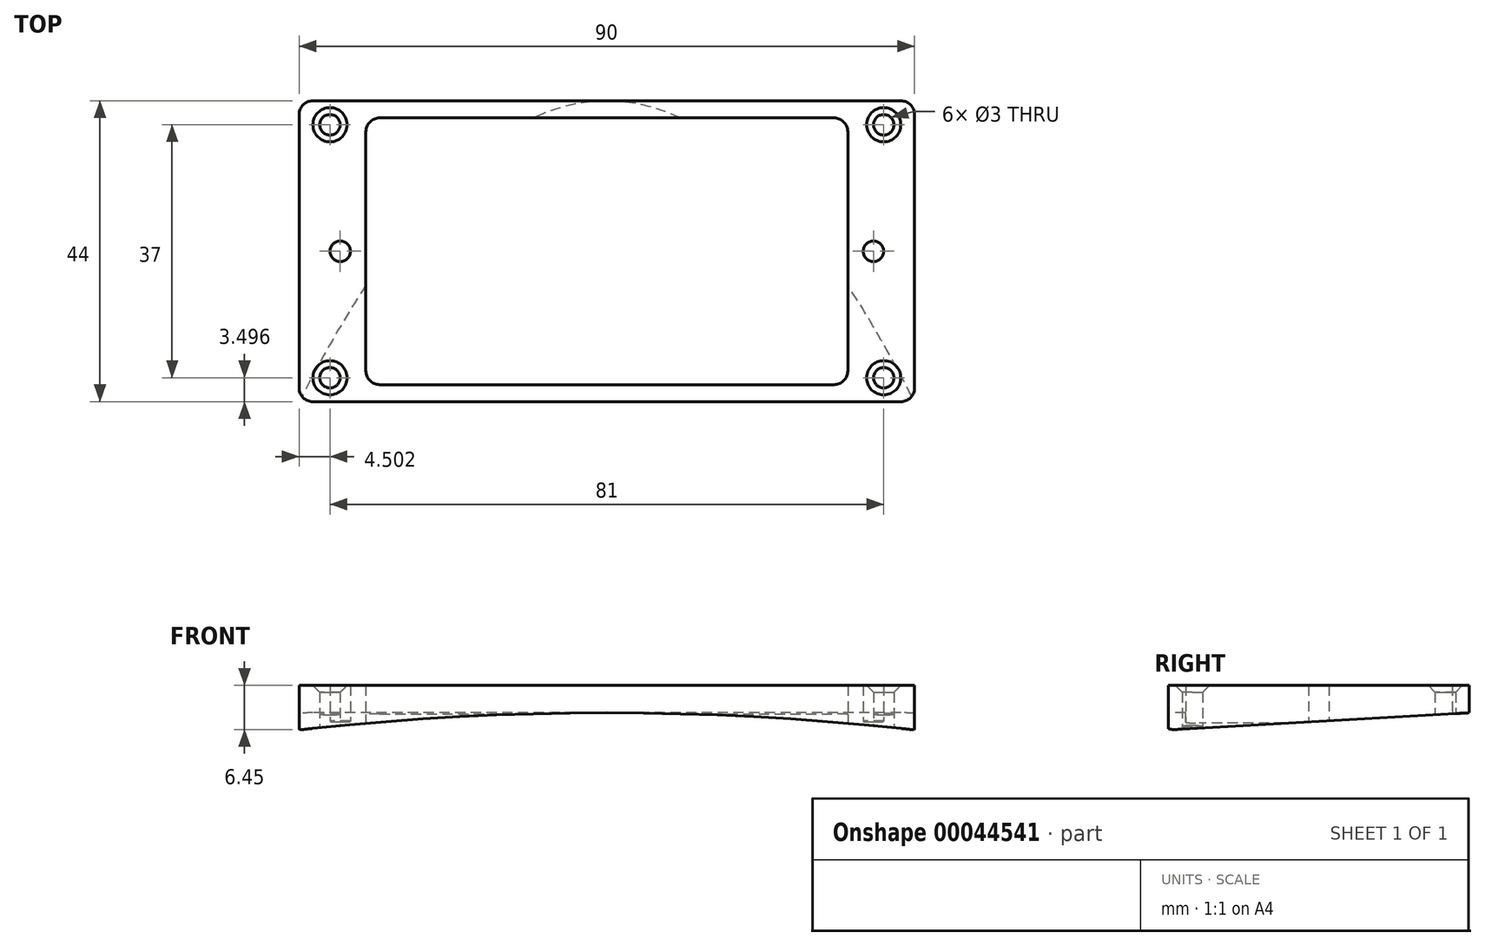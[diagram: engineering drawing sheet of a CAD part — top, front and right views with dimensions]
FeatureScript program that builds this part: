
annotation { "Feature Type Name" : "Feature", "Feature Type Description" : "" }
export const myFeature = defineFeature(function(context is Context, id is Id, definition is map)
    precondition{}
    {
        {
            var Q0;
            Q0=qCreatedBy(makeId("Top.planeOp"),FACE);
            var sketch = newSketch(context, id + "F0", { "sketchPlane" : qUnion([Q0])});
            skLineSegment(sketch, "E0.bottom", {"start": v(-26.2, 30.05) * mm, "end": v(63.8, 30.05) * mm});
            skLineSegment(sketch, "E0.top", {"start": v(-26.2, -13.95) * mm, "end": v(63.8, -13.95) * mm});
            skLineSegment(sketch, "E0.left", {"start": v(-26.2, 30.05) * mm, "end": v(-26.2, -13.95) * mm});
            skLineSegment(sketch, "E0.right", {"start": v(63.8, 30.05) * mm, "end": v(63.8, -13.95) * mm});
            skLineSegment(sketch, "E1.bottom", {"start": v(-16.45, 27.55) * mm, "end": v(54.05, 27.55) * mm});
            skLineSegment(sketch, "E1.top", {"start": v(-16.45, -11.45) * mm, "end": v(54.05, -11.45) * mm});
            skLineSegment(sketch, "E1.left", {"start": v(-16.45, 27.55) * mm, "end": v(-16.45, -11.45) * mm});
            skLineSegment(sketch, "E1.right", {"start": v(54.05, 27.55) * mm, "end": v(54.05, -11.45) * mm});
            skCircle(sketch, "E2", {"center": v(-21.7, 26.55) * mm, "radius": 1.5 * mm});
            skCircle(sketch, "E3", {"center": v(-21.7, -10.45) * mm, "radius": 1.5 * mm});
            skCircle(sketch, "E4", {"center": v(59.3, -10.45) * mm, "radius": 1.5 * mm});
            skCircle(sketch, "E5", {"center": v(59.3, 26.55) * mm, "radius": 1.5 * mm});
            skPoint(sketch, "E6", {"position": v(18.8, 30.05) * mm});
            skLineSegment(sketch, "E7", {"start": v(18.8, 30.05) * mm, "end": v(18.8, -22.23) * mm, "construction": true});
            skPoint(sketch, "E8", {"position": v(18.8, 27.55) * mm});
            skPoint(sketch, "E9", {"position": v(-26.2, 8.05) * mm});
            skLineSegment(sketch, "E10", {"start": v(-26.2, 8.05) * mm, "end": v(76.5, 8.05) * mm, "construction": true});
            skCircle(sketch, "E11", {"center": v(-20.2, 8.05) * mm, "radius": 1.5 * mm});
            skCircle(sketch, "E12", {"center": v(57.8, 8.05) * mm, "radius": 1.5 * mm});
            skPoint(sketch, "E13", {"position": v(-16.45, 8.05) * mm});
            skSolve(sketch);
        }
        {
            var Q0;
            Q0=makeQuery(id+"F0.imprint","IMPRINT",FACE,{"disambiguationData":[TD([[makeQuery(id+"F0.imprint","IMPRINT",EDGE,{"derivedFrom":sQuery(id+"F0.wireOp",EDGE,"E0.bottom")}),-1.0]])]});
            extrude(context, id + "F1", {"entities" : qUnion([Q0]), "depth" : 6.5 * mm});
        }
        {
            var Q0;
            Q0=makeQuery(id+"F1.opExtrude","SWEPT_FACE",FACE,{"disambiguationData":[OSD([sQuery(id+"F0.wireOp",EDGE,"E0.top")])]});
            var sketch = newSketch(context, id + "F2", { "sketchPlane" : qUnion([Q0])});
            skLineSegment(sketch, "E14", {"start": v(-26.2, 0) * mm, "end": v(63.8, 0) * mm});
            skLineSegment(sketch, "E15", {"start": v(-26.2, 2.5) * mm, "end": v(63.8, 2.5) * mm, "construction": true});
            skPoint(sketch, "E16", {"position": v(18.8, 2.5) * mm});
            skArc(sketch, "E17", {"start": v(63.8, 0) * mm, "mid": v(18.8, 2.5) * mm, "end": v(-26.2, 0) * mm});
            skSolve(sketch);
        }
        {
            var Q0;
            Q0=makeQuery(id+"F2.imprint","IMPRINT",FACE,{"disambiguationData":[TD([[makeQuery(id+"F2.imprint","IMPRINT",EDGE,{"derivedFrom":sQuery(id+"F2.wireOp",EDGE,"E14")}),1.0]])]});
            extrude(context, id + "F3", {"entities" : qUnion([Q0]), "operationType" : NewBodyOperationType.REMOVE, "endBound" : BoundingType.THROUGH_ALL, "oppositeDirection" : true, "depth" : 25 * mm});
        }
        {
            var Q0;
            Q0=makeQuery(id+"F1.opExtrude","CAP_EDGE",EDGE,{"disambiguationData":[OSD([sQuery(id+"F0.wireOp",EDGE,"E5")])],"isStart":false});
            var Q1;
            Q1=makeQuery(id+"F1.opExtrude","CAP_EDGE",EDGE,{"disambiguationData":[OSD([sQuery(id+"F0.wireOp",EDGE,"E2")])],"isStart":false});
            var Q2;
            Q2=makeQuery(id+"F1.opExtrude","CAP_EDGE",EDGE,{"disambiguationData":[OSD([sQuery(id+"F0.wireOp",EDGE,"E3")])],"isStart":false});
            var Q3;
            Q3=makeQuery(id+"F1.opExtrude","CAP_EDGE",EDGE,{"disambiguationData":[OSD([sQuery(id+"F0.wireOp",EDGE,"E4")])],"isStart":false});
            chamfer(context, id + "F4", {"entities" : qUnion([Q0, Q1, Q2, Q3]), "width" : 1 * mm, "tangentPropagation" : true});
        }
        {
            var Q0;
            Q0=makeQuery(id+"F1.opExtrude","SWEPT_FACE",FACE,{"disambiguationData":[OSD([sQuery(id+"F0.wireOp",EDGE,"E0.left")])]});
            var sketch = newSketch(context, id + "F5", { "sketchPlane" : qUnion([Q0])});
            skLineSegment(sketch, "E18", {"start": v(-30.05, 2.5) * mm, "end": v(-30.05, 0) * mm});
            skLineSegment(sketch, "E19", {"start": v(-30.05, 0) * mm, "end": v(13.95, 0) * mm});
            skLineSegment(sketch, "E20", {"start": v(13.95, 0) * mm, "end": v(-30.05, 2.5) * mm});
            skSolve(sketch);
        }
        {
            var Q0;
            Q0=makeQuery(id+"F1.opExtrude","SWEPT_EDGE",EDGE,{"disambiguationData":[OSD([sQuery(id+"F0.wireOp",EDGE,"E1.bottom"),sQuery(id+"F0.wireOp",EDGE,"E1.left")])]});
            var Q1;
            Q1=makeQuery(id+"F1.opExtrude","SWEPT_EDGE",EDGE,{"disambiguationData":[OSD([sQuery(id+"F0.wireOp",EDGE,"E1.bottom"),sQuery(id+"F0.wireOp",EDGE,"E1.right")])]});
            var Q2;
            Q2=makeQuery(id+"F1.opExtrude","SWEPT_EDGE",EDGE,{"disambiguationData":[OSD([sQuery(id+"F0.wireOp",EDGE,"E1.top"),sQuery(id+"F0.wireOp",EDGE,"E1.right")])]});
            var Q3;
            Q3=makeQuery(id+"F1.opExtrude","SWEPT_EDGE",EDGE,{"disambiguationData":[OSD([sQuery(id+"F0.wireOp",EDGE,"E1.top"),sQuery(id+"F0.wireOp",EDGE,"E1.left")])]});
            var Q4;
            Q4=makeQuery(id+"F1.opExtrude","SWEPT_EDGE",EDGE,{"disambiguationData":[OSD([sQuery(id+"F0.wireOp",EDGE,"E0.bottom"),sQuery(id+"F0.wireOp",EDGE,"E0.right")])]});
            var Q5;
            Q5=makeQuery(id+"F1.opExtrude","SWEPT_EDGE",EDGE,{"disambiguationData":[OSD([sQuery(id+"F0.wireOp",EDGE,"E0.top"),sQuery(id+"F0.wireOp",EDGE,"E0.right")])]});
            var Q6;
            Q6=makeQuery(id+"F1.opExtrude","SWEPT_EDGE",EDGE,{"disambiguationData":[OSD([sQuery(id+"F0.wireOp",EDGE,"E0.bottom"),sQuery(id+"F0.wireOp",EDGE,"E0.left")])]});
            var Q7;
            Q7=makeQuery(id+"F1.opExtrude","SWEPT_EDGE",EDGE,{"disambiguationData":[OSD([sQuery(id+"F0.wireOp",EDGE,"E0.top"),sQuery(id+"F0.wireOp",EDGE,"E0.left")])]});
            fillet(context, id + "F6", {"entities" : qUnion([Q0, Q1, Q2, Q3, Q4, Q5, Q6, Q7]), "radius" : 2 * mm, "tangentPropagation" : true, "allowEdgeOverflow" : false});
        }
        {
            var Q0;
            Q0=makeQuery(id+"F5.imprint","IMPRINT",FACE,{"disambiguationData":[TD([[makeQuery(id+"F5.imprint","IMPRINT",EDGE,{"derivedFrom":sQuery(id+"F5.wireOp",EDGE,"E18")}),1.0]])]});
            extrude(context, id + "F7", {"entities" : qUnion([Q0]), "operationType" : NewBodyOperationType.REMOVE, "endBound" : BoundingType.THROUGH_ALL, "oppositeDirection" : true, "depth" : 25 * mm});
        }
    });
